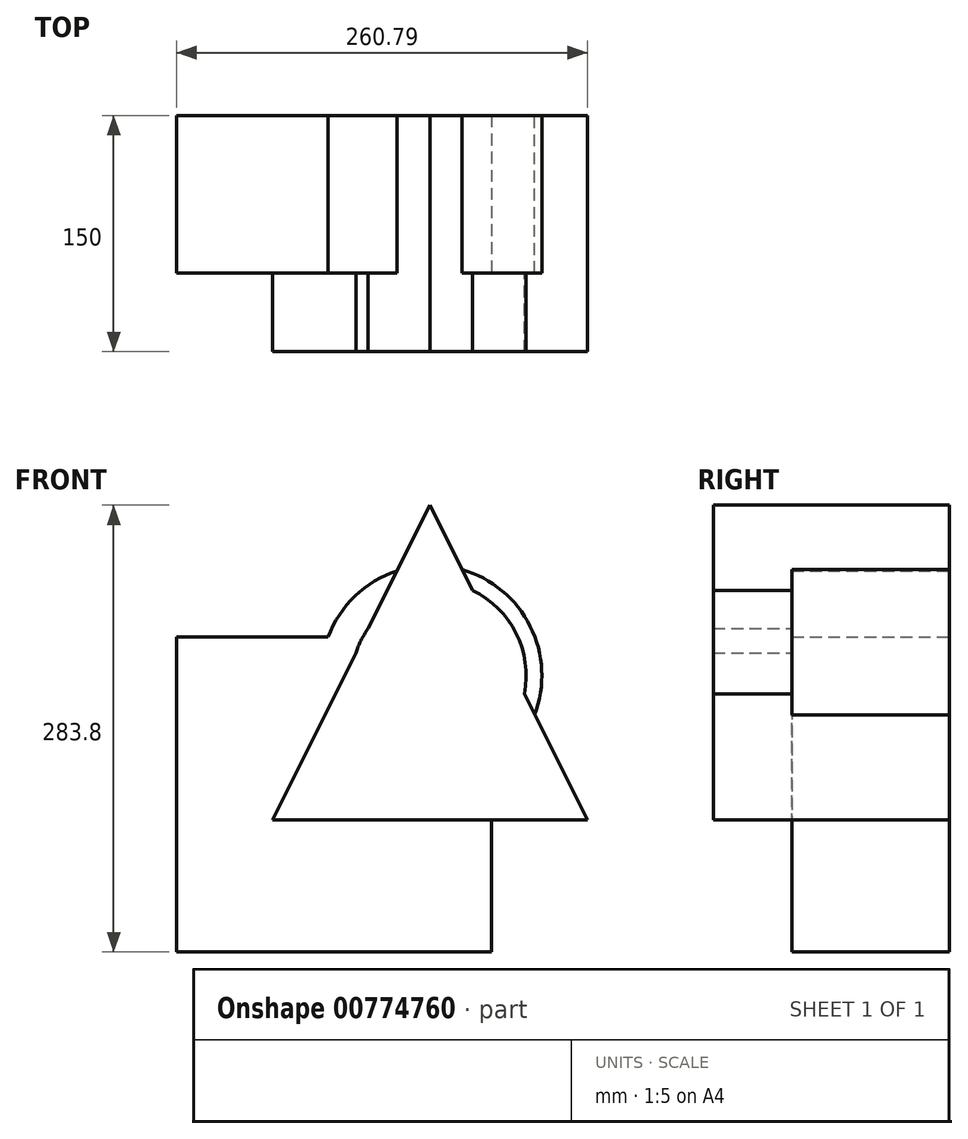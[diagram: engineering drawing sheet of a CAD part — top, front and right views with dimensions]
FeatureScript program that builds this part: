
annotation { "Feature Type Name" : "Feature", "Feature Type Description" : "" }
export const myFeature = defineFeature(function(context is Context, id is Id, definition is map)
    precondition{}
    {
        {
            var Q0;
            Q0=qCreatedBy(makeId("Front.planeOp"),FACE);
            var sketch = newSketch(context, id + "F0", { "sketchPlane" : qUnion([Q0])});
            skLineSegment(sketch, "E0", {"start": v(-39.2, -16.2) * mm, "end": v(160.8, -16.2) * mm});
            skLineSegment(sketch, "E1", {"start": v(60.8, 183.8) * mm, "end": v(160.8, -16.2) * mm});
            skLineSegment(sketch, "E2", {"start": v(60.8, 183.8) * mm, "end": v(-39.2, -16.2) * mm});
            skPoint(sketch, "E3.start.orphan", {"position": v(60.8, -16.2) * mm});
            skCircle(sketch, "E4", {"center": v(61.81, 75.53) * mm, "radius": 70.09 * mm});
            skSolve(sketch);
        }
        {
            var Q0;
            Q0 = qSketchRegion(id + "F0", true);
            extrude(context, id + "F1", {"entities" : qUnion([Q0]), "depth" : 50 * mm, "offsetDistance" : 25 * mm});
        }
        {
            var Q0;
            {var subQ0=sQuery(id+"F0.wireOp",EDGE,"E4");var subQ1=sQuery(id+"F0.wireOp",EDGE,"E1");Q0=makeQuery(id+"F1.opExtrude","CAP_EDGE",EDGE,{"disambiguationData":[OSD([subQ0]),TDD([makeQuery(id+"F0.imprint","IMPRINT",EDGE,{"disambiguationData":[TD([[makeQuery(id+"F0.imprint","INTERSECT",VERTEX,{"disambiguationData":[OD(0.0)],"derivedFrom":[subQ1,subQ0]}),1.0]])],"derivedFrom":subQ0})])],"isStart":false});}
            fillet(context, id + "F2", {"entities" : qUnion([Q0]), "radius" : 10 * mm, "tangentPropagation" : true, "allowEdgeOverflow" : false});
        }
        {
            var Q0;
            {var subQ0=sQuery(id+"F0.wireOp",EDGE,"E4");var subQ1=sQuery(id+"F0.wireOp",EDGE,"E2");Q0=makeQuery(id+"F1.opExtrude","CAP_EDGE",EDGE,{"disambiguationData":[OSD([subQ0]),TDD([makeQuery(id+"F0.imprint","IMPRINT",EDGE,{"disambiguationData":[TD([[makeQuery(id+"F0.imprint","INTERSECT",VERTEX,{"disambiguationData":[OD(0.0)],"derivedFrom":[subQ1,subQ0]}),-1.0]])],"derivedFrom":subQ0})])],"isStart":false});}
            fillet(context, id + "F3", {"entities" : qUnion([Q0]), "radius" : 20 * mm, "tangentPropagation" : true, "allowEdgeOverflow" : false});
        }
        {
            var Q0;
            Q0=qCreatedBy(makeId("Front.planeOp"),FACE);
            var sketch = newSketch(context, id + "F4", { "sketchPlane" : qUnion([Q0])});
            skLineSegment(sketch, "E5.bottom", {"start": v(100, -100) * mm, "end": v(-100, -100) * mm});
            skLineSegment(sketch, "E5.top", {"start": v(100, 100) * mm, "end": v(-100, 100) * mm});
            skLineSegment(sketch, "E5.left", {"start": v(100, -100) * mm, "end": v(100, 100) * mm});
            skLineSegment(sketch, "E5.right", {"start": v(-100, -100) * mm, "end": v(-100, 100) * mm});
            skPoint(sketch, "E5.middle", {"position": v(0, 0) * mm});
            skSolve(sketch);
        }
        {
            var Q0;
            Q0=makeQuery(id+"F4.imprint","IMPRINT",FACE,{"disambiguationData":[TD([[makeQuery(id+"F4.imprint","IMPRINT",EDGE,{"derivedFrom":sQuery(id+"F4.wireOp",EDGE,"E5.bottom")}),-1.0]])]});
            var Q1;
            Q1=makeQuery(id+"F1.opExtrude","CAP_FACE",FACE,{"disambiguationData":[OSD([sQuery(id+"F0.wireOp",EDGE,"E0"),sQuery(id+"F0.wireOp",EDGE,"E1"),sQuery(id+"F0.wireOp",EDGE,"E2"),sQuery(id+"F0.wireOp",EDGE,"E4")])],"isStart":false});
            var Q2;
            Q2=makeQuery(id+"F1.opExtrude","CAP_FACE",FACE,{"disambiguationData":[OSD([sQuery(id+"F0.wireOp",EDGE,"E0"),sQuery(id+"F0.wireOp",EDGE,"E1"),sQuery(id+"F0.wireOp",EDGE,"E2"),sQuery(id+"F0.wireOp",EDGE,"E4")])],"isStart":true});
            extrude(context, id + "F5", {"entities" : qUnion([Q0, Q1, Q2]), "operationType" : NewBodyOperationType.ADD, "depth" : 100 * mm, "offsetDistance" : 25 * mm});
        }
    });
